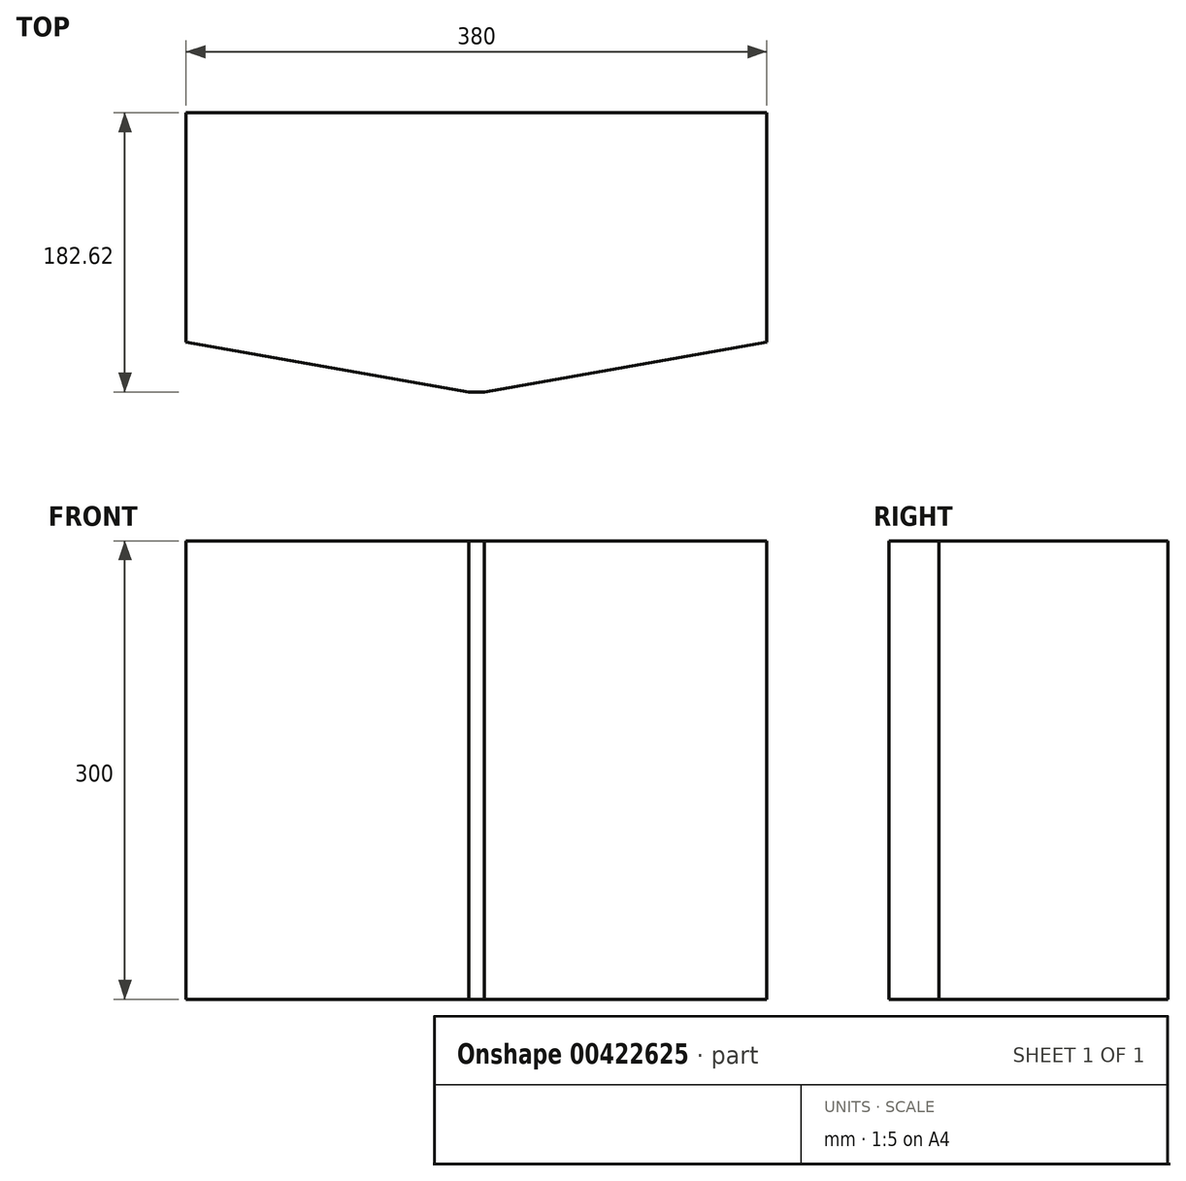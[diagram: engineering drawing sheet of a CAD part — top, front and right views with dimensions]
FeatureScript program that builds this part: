
annotation { "Feature Type Name" : "Feature", "Feature Type Description" : "" }
export const myFeature = defineFeature(function(context is Context, id is Id, definition is map)
    precondition{}
    {
        {
            var Q0;
            Q0=qCreatedBy(makeId("Top.planeOp"),FACE);
            var sketch = newSketch(context, id + "F0", { "sketchPlane" : qUnion([Q0])});
            skLineSegment(sketch, "E0", {"start": v(0, 0) * mm, "end": v(380, 0) * mm});
            skLineSegment(sketch, "E1", {"start": v(0, 0) * mm, "end": v(0, -150) * mm});
            skLineSegment(sketch, "E2", {"start": v(0, -150) * mm, "end": v(185, -182.62) * mm});
            skLineSegment(sketch, "E3", {"start": v(380, 0) * mm, "end": v(380, -150) * mm});
            skLineSegment(sketch, "E4", {"start": v(380, -150) * mm, "end": v(195, -182.62) * mm});
            skLineSegment(sketch, "E5", {"start": v(185, -182.62) * mm, "end": v(195, -182.62) * mm});
            skLineSegment(sketch, "E6", {"start": v(0, 0) * mm, "end": v(-10, 0) * mm});
            skLineSegment(sketch, "E7", {"start": v(-10, 0) * mm, "end": v(-10, -150) * mm});
            skLineSegment(sketch, "E8", {"start": v(-10, -150) * mm, "end": v(0, -150) * mm});
            skLineSegment(sketch, "E9", {"start": v(0, -10) * mm, "end": v(380, -10) * mm});
            skLineSegment(sketch, "E10", {"start": v(185, -182.62) * mm, "end": v(183.26, -192.47) * mm, "construction": true});
            skLineSegment(sketch, "E11", {"start": v(183.26, -192.47) * mm, "end": v(-11.43, -158.14) * mm, "construction": true});
            skLineSegment(sketch, "E12", {"start": v(-10, -150) * mm, "end": v(-10, -158.4) * mm});
            skLineSegment(sketch, "E13", {"start": v(-10, -158.4) * mm, "end": v(183.26, -192.47) * mm});
            skLineSegment(sketch, "E14", {"start": v(0, -150) * mm, "end": v(-9.7, -148.29) * mm, "construction": true});
            skLineSegment(sketch, "E15", {"start": v(-11.43, -158.14) * mm, "end": v(-9.7, -148.29) * mm, "construction": true});
            skLineSegment(sketch, "E16", {"start": v(183.26, -192.47) * mm, "end": v(185, -192.77) * mm, "construction": true});
            skLineSegment(sketch, "E17", {"start": v(185, -182.62) * mm, "end": v(185, -192.77) * mm});
            skLineSegment(sketch, "E18", {"start": v(185, -192.77) * mm, "end": v(186.74, -182.93) * mm, "construction": true});
            skLineSegment(sketch, "E19", {"start": v(185, -182.62) * mm, "end": v(186.74, -182.93) * mm, "construction": true});
            skLineSegment(sketch, "E20", {"start": v(190, -182.62) * mm, "end": v(190, -10) * mm, "construction": true});
            skLineSegment(sketch, "E21.MirrorCS", {"start": v(195, -192.77) * mm, "end": v(193.26, -182.93) * mm, "construction": true});
            skLineSegment(sketch, "E22.MirrorCS", {"start": v(195, -182.62) * mm, "end": v(193.26, -182.93) * mm, "construction": true});
            skLineSegment(sketch, "E23.MirrorCS", {"start": v(195, -182.62) * mm, "end": v(195, -192.77) * mm});
            skLineSegment(sketch, "E24.MirrorCS", {"start": v(196.74, -192.47) * mm, "end": v(195, -192.77) * mm, "construction": true});
            skLineSegment(sketch, "E25.MirrorCS", {"start": v(195, -182.62) * mm, "end": v(196.74, -192.47) * mm, "construction": true});
            skLineSegment(sketch, "E26.MirrorCS", {"start": v(196.74, -192.47) * mm, "end": v(391.43, -158.14) * mm, "construction": true});
            skLineSegment(sketch, "E27.MirrorCS", {"start": v(390, -150) * mm, "end": v(390, -158.4) * mm});
            skLineSegment(sketch, "E28.MirrorCS", {"start": v(391.43, -158.14) * mm, "end": v(389.7, -148.29) * mm, "construction": true});
            skLineSegment(sketch, "E29.MirrorCS", {"start": v(380, -150) * mm, "end": v(389.7, -148.29) * mm, "construction": true});
            skLineSegment(sketch, "E30", {"start": v(-10, -158.4) * mm, "end": v(185, -192.77) * mm});
            skLineSegment(sketch, "E31", {"start": v(185, -192.77) * mm, "end": v(195, -192.77) * mm});
            skLineSegment(sketch, "E32", {"start": v(195, -182.62) * mm, "end": v(195, -62.62) * mm});
            skLineSegment(sketch, "E33", {"start": v(195, -62.62) * mm, "end": v(185, -62.62) * mm});
            skLineSegment(sketch, "E34", {"start": v(185, -62.62) * mm, "end": v(185, -182.62) * mm});
            skLineSegment(sketch, "E35", {"start": v(380, 0) * mm, "end": v(390, 0) * mm});
            skLineSegment(sketch, "E36", {"start": v(390, 0) * mm, "end": v(390, -150) * mm});
            skLineSegment(sketch, "E37", {"start": v(380, -150) * mm, "end": v(390, -150) * mm});
            skLineSegment(sketch, "E38", {"start": v(195, -192.77) * mm, "end": v(390, -158.4) * mm});
            skSolve(sketch);
        }
        {
            var Q0;
            Q0=makeQuery(id+"F0.imprint","IMPRINT",FACE,{"disambiguationData":[TD([[makeQuery(id+"F0.imprint","IMPRINT",EDGE,{"derivedFrom":sQuery(id+"F0.wireOp",EDGE,"E0")}),-1.0]])]});
            var Q1;
            {var subQ3=sQuery(id+"F0.wireOp",EDGE,"E2");Q1=makeQuery(id+"F0.imprint","IMPRINT",FACE,{"disambiguationData":[TD([[makeQuery(id+"F0.imprint","IMPRINT",EDGE,{"derivedFrom":subQ3}),1.0]])]});}
            var Q2;
            Q2=makeQuery(id+"F0.imprint","IMPRINT",FACE,{"disambiguationData":[TD([[makeQuery(id+"F0.imprint","IMPRINT",EDGE,{"derivedFrom":sQuery(id+"F0.wireOp",EDGE,"E5")}),1.0]])]});
            extrude(context, id + "F1", {"entities" : qUnion([Q0, Q1, Q2]), "depth" : 300 * mm});
        }
        {
            var Q0;
            Q0=makeQuery(id+"F1.opExtrude","SWEPT_FACE",FACE,{"disambiguationData":[OSD([sQuery(id+"F0.wireOp",EDGE,"E3")])]});
            var sketch = newSketch(context, id + "F2", { "sketchPlane" : qUnion([Q0])});
            skLineSegment(sketch, "E39", {"start": v(0, 0) * mm, "end": v(-58.31, 300) * mm});
            skLineSegment(sketch, "E40", {"start": v(-58.31, 300) * mm, "end": v(0, 300) * mm});
            skLineSegment(sketch, "E41", {"start": v(0, 300) * mm, "end": v(0, 0) * mm});
            skSolve(sketch);
        }
    });
